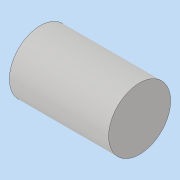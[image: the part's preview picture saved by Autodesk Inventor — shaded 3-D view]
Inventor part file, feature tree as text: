
AUTODESK INVENTOR PART (.ipt)
format: ipt  version: 2019 (Build 230136000, 136)  size: 79,872 bytes
history: native  units: mm
features: other x1, extrude x1, sketch x1
ambient origin geometry x8: Origin, YZ Plane, XZ Plane, XY Plane, X Axis, Y Axis, Z Axis, Center Point
bodies: Body1 (feature_tree)
feature tree (3):
  other  "Твердое тело1"
  extrude  "Выдавливание1"  Depth=50.0mm
  sketch  "Эскиз1"
